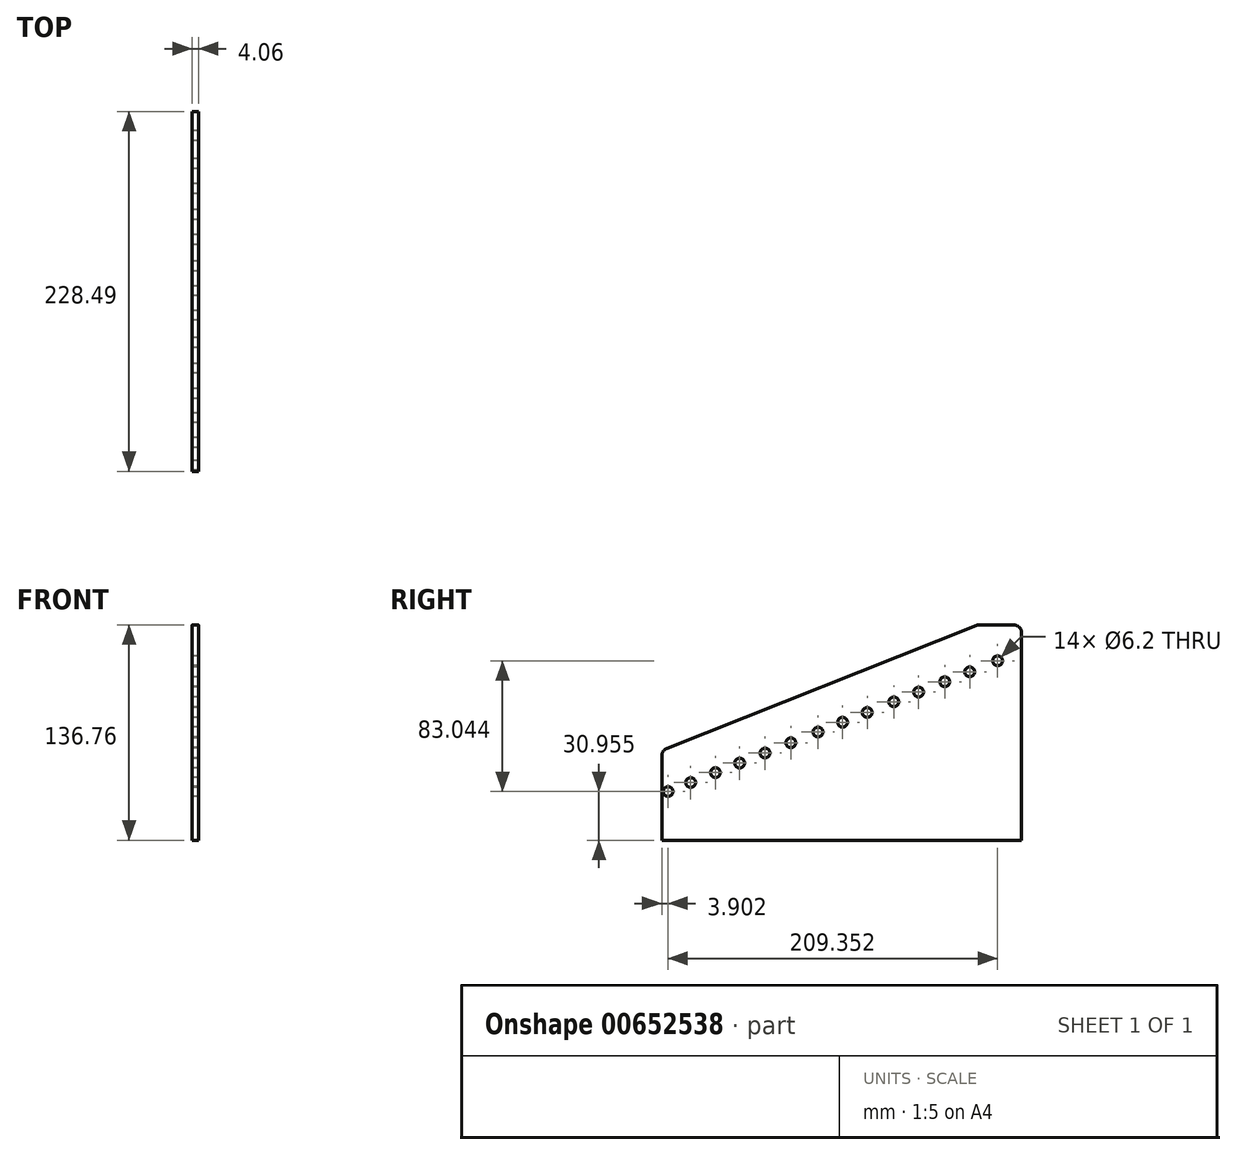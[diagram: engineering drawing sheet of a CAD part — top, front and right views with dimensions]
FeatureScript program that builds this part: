
annotation { "Feature Type Name" : "Feature", "Feature Type Description" : "" }
export const myFeature = defineFeature(function(context is Context, id is Id, definition is map)
    precondition{}
    {
        {
            var Q0;
            Q0=qCreatedBy(makeId("Right.planeOp"),FACE);
            var sketch = newSketch(context, id + "F0", { "sketchPlane" : qUnion([Q0])});
            skLineSegment(sketch, "E0", {"start": v(-110.35, -51.46) * mm, "end": v(118.14, -51.46) * mm});
            skLineSegment(sketch, "E1", {"start": v(118.14, -51.46) * mm, "end": v(118.14, 85.3) * mm});
            skLineSegment(sketch, "E2", {"start": v(118.14, 85.3) * mm, "end": v(90.28, 85.3) * mm});
            skLineSegment(sketch, "E3", {"start": v(90.28, 85.3) * mm, "end": v(-110.35, 5.71) * mm});
            skLineSegment(sketch, "E4", {"start": v(-110.35, 5.71) * mm, "end": v(-110.35, -51.46) * mm});
            skCircle(sketch, "E5", {"center": v(102.9, 62.54) * mm, "radius": 3.1 * mm});
            skCircle(sketch, "E6", {"center": v(85.14, 55.5) * mm, "radius": 3.1 * mm});
            skCircle(sketch, "E7", {"center": v(69.27, 49.2) * mm, "radius": 3.1 * mm});
            skCircle(sketch, "E8", {"center": v(52.71, 42.63) * mm, "radius": 3.1 * mm});
            skCircle(sketch, "E9", {"center": v(36.97, 36.38) * mm, "radius": 3.1 * mm});
            skCircle(sketch, "E10", {"center": v(20.04, 29.67) * mm, "radius": 3.1 * mm});
            skCircle(sketch, "E11", {"center": v(4.42, 23.47) * mm, "radius": 3.1 * mm});
            skCircle(sketch, "E12", {"center": v(-11.2, 17.27) * mm, "radius": 3.1 * mm});
            skCircle(sketch, "E13", {"center": v(-28.43, 10.44) * mm, "radius": 3.1 * mm});
            skCircle(sketch, "E14", {"center": v(-44.87, 3.92) * mm, "radius": 3.1 * mm});
            skCircle(sketch, "E15", {"center": v(-60.96, -2.46) * mm, "radius": 3.1 * mm});
            skCircle(sketch, "E16", {"center": v(-76.34, -8.56) * mm, "radius": 3.1 * mm});
            skCircle(sketch, "E17", {"center": v(-92.08, -14.8) * mm, "radius": 3.1 * mm});
            skCircle(sketch, "E18", {"center": v(-106.45, -20.5) * mm, "radius": 3.1 * mm});
            skSolve(sketch);
        }
        {
            var Q0;
            Q0=makeQuery(id+"F0.imprint","IMPRINT",FACE,{"disambiguationData":[TD([[makeQuery(id+"F0.imprint","IMPRINT",EDGE,{"derivedFrom":sQuery(id+"F0.wireOp",EDGE,"E0")}),1.0]])]});
            extrude(context, id + "F1", {"entities" : qUnion([Q0]), "depth" : 4.06 * mm, "offsetDistance" : 25.4 * mm});
        }
        {
            var Q0;
            Q0=makeQuery(id+"F1.opExtrude","SWEPT_EDGE",EDGE,{"disambiguationData":[OSD([sQuery(id+"F0.wireOp",EDGE,"E3"),sQuery(id+"F0.wireOp",EDGE,"E4")])]});
            var Q1;
            Q1=makeQuery(id+"F1.opExtrude","SWEPT_EDGE",EDGE,{"disambiguationData":[OSD([sQuery(id+"F0.wireOp",EDGE,"E1"),sQuery(id+"F0.wireOp",EDGE,"E2")])]});
            var Q2;
            Q2=makeQuery(id+"F1.opExtrude","SWEPT_EDGE",EDGE,{"disambiguationData":[OSD([sQuery(id+"F0.wireOp",EDGE,"E2"),sQuery(id+"F0.wireOp",EDGE,"E3")])]});
            fillet(context, id + "F2", {"entities" : qUnion([Q0, Q1, Q2]), "radius" : 5.08 * mm, "tangentPropagation" : true, "allowEdgeOverflow" : false});
        }
    });
